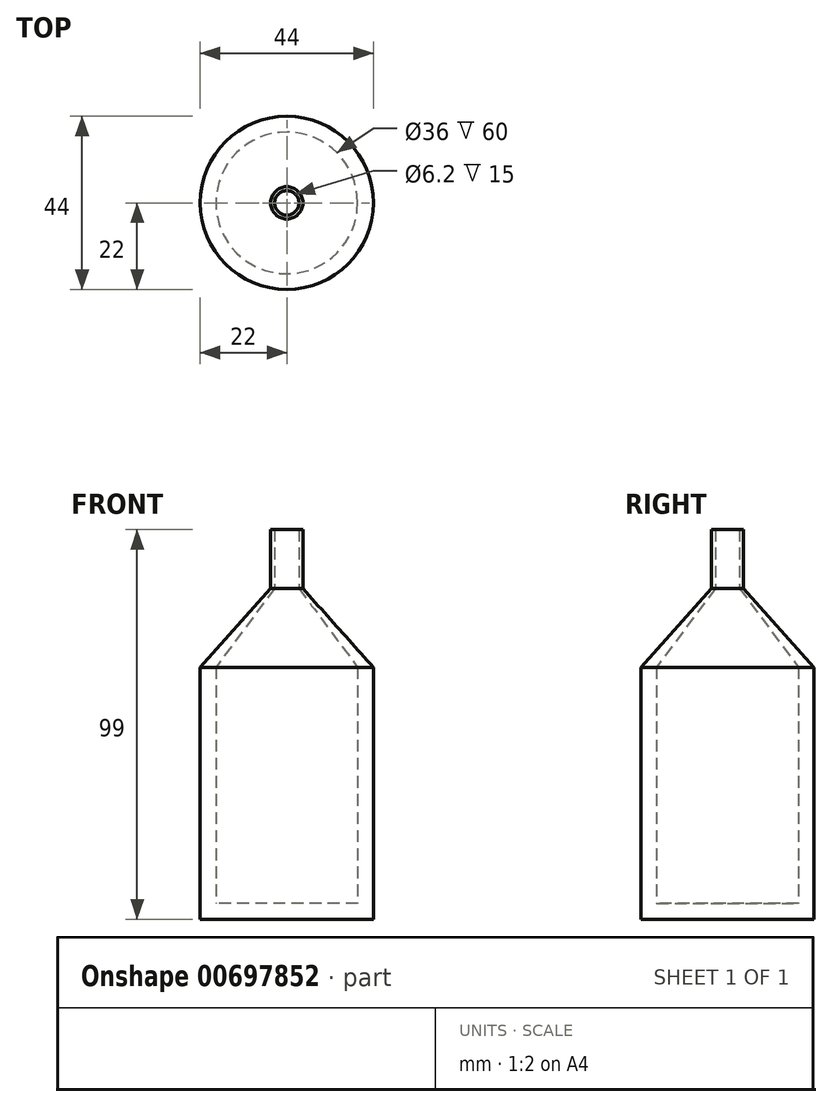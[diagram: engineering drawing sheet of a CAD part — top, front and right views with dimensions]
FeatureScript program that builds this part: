
annotation { "Feature Type Name" : "Feature", "Feature Type Description" : "" }
export const myFeature = defineFeature(function(context is Context, id is Id, definition is map)
    precondition{}
    {
        {
            assignVariable(context, id + "F0", {"name" : "W", "anyValue" : 2});
        }
        {
            var Q0;
            Q0=qCreatedBy(makeId("Top.planeOp"),FACE);
            var sketch = newSketch(context, id + "F1", { "sketchPlane" : qUnion([Q0])});
            skCircle(sketch, "E0", {"center": v(0, 0) * mm, "radius": 20 * mm, "construction": true});
            skArc(sketch, "E1.0", {"start": v(-11.23, -14.06) * mm, "mid": v(-6.89, -16.63) * mm, "end": v(-2, -17.89) * mm});
            skLineSegment(sketch, "E2", {"start": v(0, 0) * mm, "end": v(0, 18) * mm, "construction": true});
            skLineSegment(sketch, "E3", {"start": v(0, 0) * mm, "end": v(18, 0) * mm, "construction": true});
            skLineSegment(sketch, "E4", {"start": v(0, 0) * mm, "end": v(0, -18) * mm, "construction": true});
            skLineSegment(sketch, "E5", {"start": v(0, 0) * mm, "end": v(-18, 0) * mm, "construction": true});
            skLineSegment(sketch, "E6", {"start": v(0, 0) * mm, "end": v(-12.73, 12.73) * mm, "construction": true});
            skLineSegment(sketch, "E7", {"start": v(0, 0) * mm, "end": v(12.73, 12.73) * mm, "construction": true});
            skLineSegment(sketch, "E8", {"start": v(0, 0) * mm, "end": v(12.73, -12.73) * mm, "construction": true});
            skLineSegment(sketch, "E9", {"start": v(0, 0) * mm, "end": v(-12.73, -12.73) * mm, "construction": true});
            skCircle(sketch, "E10.0", {"center": v(0, 0) * mm, "radius": 22 * mm});
            skArc(sketch, "E11.0", {"start": v(-14.08, -16.9) * mm, "mid": v(-8.42, -20.33) * mm, "end": v(-2, -21.9) * mm});
            skCircle(sketch, "E12.0", {"center": v(0, 0) * mm, "radius": 18 * mm});
            skLineSegment(sketch, "E13.0", {"start": v(-17.89, 2) * mm, "end": v(-21.9, 2) * mm});
            skLineSegment(sketch, "E14.0", {"start": v(-17.89, -2) * mm, "end": v(-21.9, -2) * mm});
            skLineSegment(sketch, "E15.0", {"start": v(2, 17.89) * mm, "end": v(2, 21.9) * mm});
            skLineSegment(sketch, "E16.0", {"start": v(-2, 17.89) * mm, "end": v(-2, 21.9) * mm});
            skLineSegment(sketch, "E17.0", {"start": v(-11.23, 14.06) * mm, "end": v(-14.08, 16.9) * mm});
            skLineSegment(sketch, "E18.0", {"start": v(-14.06, 11.23) * mm, "end": v(-16.9, 14.08) * mm});
            skLineSegment(sketch, "E19.0", {"start": v(-14.06, -11.23) * mm, "end": v(-16.9, -14.08) * mm});
            skLineSegment(sketch, "E20.0", {"start": v(-11.23, -14.06) * mm, "end": v(-14.08, -16.9) * mm});
            skLineSegment(sketch, "E21.0", {"start": v(2, -17.89) * mm, "end": v(2, -21.9) * mm});
            skLineSegment(sketch, "E22.0", {"start": v(11.23, -14.06) * mm, "end": v(14.08, -16.9) * mm});
            skLineSegment(sketch, "E23.0", {"start": v(-2, -17.89) * mm, "end": v(-2, -21.9) * mm});
            skLineSegment(sketch, "E24.0", {"start": v(14.06, -11.23) * mm, "end": v(16.9, -14.08) * mm});
            skLineSegment(sketch, "E25.0", {"start": v(17.89, -2) * mm, "end": v(21.9, -2) * mm});
            skLineSegment(sketch, "E26.0", {"start": v(17.89, 2) * mm, "end": v(21.9, 2) * mm});
            skLineSegment(sketch, "E27.0", {"start": v(14.06, 11.23) * mm, "end": v(16.9, 14.08) * mm});
            skLineSegment(sketch, "E28.0", {"start": v(11.23, 14.06) * mm, "end": v(14.08, 16.9) * mm});
            skArc(sketch, "E29.trimOffspring", {"start": v(2, -17.89) * mm, "mid": v(6.89, -16.63) * mm, "end": v(11.23, -14.06) * mm});
            skArc(sketch, "E30.trimOffspring", {"start": v(2, -21.9) * mm, "mid": v(8.42, -20.33) * mm, "end": v(14.08, -16.9) * mm});
            skArc(sketch, "E31.trimOffspring", {"start": v(16.9, -14.08) * mm, "mid": v(20.33, -8.42) * mm, "end": v(21.9, -2) * mm});
            skArc(sketch, "E32.trimOffspring", {"start": v(14.06, -11.23) * mm, "mid": v(16.63, -6.89) * mm, "end": v(17.89, -2) * mm});
            skArc(sketch, "E33.trimOffspring", {"start": v(17.89, 2) * mm, "mid": v(16.63, 6.89) * mm, "end": v(14.06, 11.23) * mm});
            skArc(sketch, "E34.trimOffspring", {"start": v(21.9, 2) * mm, "mid": v(20.33, 8.42) * mm, "end": v(16.9, 14.08) * mm});
            skArc(sketch, "E35.trimOffspring", {"start": v(14.08, 16.9) * mm, "mid": v(8.42, 20.33) * mm, "end": v(2, 21.9) * mm});
            skArc(sketch, "E36.trimOffspring", {"start": v(11.23, 14.06) * mm, "mid": v(6.89, 16.63) * mm, "end": v(2, 17.89) * mm});
            skArc(sketch, "E37.trimOffspring", {"start": v(-2, 21.9) * mm, "mid": v(-8.42, 20.33) * mm, "end": v(-14.08, 16.9) * mm});
            skArc(sketch, "E38.trimOffspring", {"start": v(-2, 17.89) * mm, "mid": v(-6.89, 16.63) * mm, "end": v(-11.23, 14.06) * mm});
            skArc(sketch, "E39.trimOffspring", {"start": v(-14.06, 11.23) * mm, "mid": v(-16.63, 6.89) * mm, "end": v(-17.89, 2) * mm});
            skArc(sketch, "E40.trimOffspring", {"start": v(-16.9, 14.08) * mm, "mid": v(-20.33, 8.42) * mm, "end": v(-21.9, 2) * mm});
            skArc(sketch, "E41.trimOffspring", {"start": v(-17.89, -2) * mm, "mid": v(-16.63, -6.89) * mm, "end": v(-14.06, -11.23) * mm});
            skArc(sketch, "E42.trimOffspring", {"start": v(-21.9, -2) * mm, "mid": v(-20.33, -8.42) * mm, "end": v(-16.9, -14.08) * mm});
            skSolve(sketch);
        }
        {
            var Q0;
            Q0 = qSketchRegion(id + "F1", true);
            extrude(context, id + "F2", {"entities" : qUnion([Q0]), "depth" : (getVariable(context, 'W')) * mm, "offsetDistance" : 25 * mm});
        }
        {
            var Q0;
            Q0=qCreatedBy(makeId("Top.planeOp"),FACE);
            var sketch = newSketch(context, id + "F3", { "sketchPlane" : qUnion([Q0])});
            skCircle(sketch, "E43.0", {"center": v(0, 0) * mm, "radius": 22 * mm});
            skCircle(sketch, "E44.0", {"center": v(0, 0) * mm, "radius": 18 * mm});
            skSolve(sketch);
        }
        {
            var Q0;
            Q0 = qSketchRegion(id + "F3", true);
            extrude(context, id + "F4", {"entities" : qUnion([Q0]), "operationType" : NewBodyOperationType.ADD, "depth" : 60 * mm, "offsetDistance" : 25 * mm});
        }
        {
            var Q0;
            Q0=qCreatedBy(makeId("Top.planeOp"),FACE);
            var sketch = newSketch(context, id + "F5", { "sketchPlane" : qUnion([Q0])});
            skCircle(sketch, "E45.0", {"center": v(0, 0) * mm, "radius": 22 * mm});
            skSolve(sketch);
        }
        {
            var Q0;
            Q0 = qSketchRegion(id + "F5", true);
            extrude(context, id + "F6", {"entities" : qUnion([Q0]), "operationType" : NewBodyOperationType.ADD, "oppositeDirection" : true, "depth" : (getVariable(context, 'W') * 2) * mm, "offsetDistance" : 25 * mm});
        }
        {
            var Q0;
            Q0=makeQuery(id+"F4.opExtrude","CAP_FACE",FACE,{"disambiguationData":[OSD([sQuery(id+"F3.wireOp",EDGE,"E43.0"),sQuery(id+"F3.wireOp",EDGE,"E44.0")])],"isStart":false});
            cPlane(context, id + "F7", {"entities" : qUnion([Q0]), "cplaneType" : CPlaneType.OFFSET, "offset" : 20 * mm, "width" : 150 * mm, "height" : 150 * mm});
        }
        {
            var Q0;
            Q0=qCreatedBy(id+"F7.planeOp",FACE);
            var sketch = newSketch(context, id + "F8", { "sketchPlane" : qUnion([Q0])});
            skCircle(sketch, "E46", {"center": v(0, 0) * mm, "radius": 4.1 * mm});
            skSolve(sketch);
        }
        {
            var Q0;
            Q0=makeQuery(id+"F4.opExtrude","CAP_FACE",FACE,{"disambiguationData":[OSD([sQuery(id+"F3.wireOp",EDGE,"E43.0"),sQuery(id+"F3.wireOp",EDGE,"E44.0")])],"isStart":false});
            cPlane(context, id + "F9", {"entities" : qUnion([Q0]), "cplaneType" : CPlaneType.OFFSET, "offset" : 0 * mm, "width" : 150 * mm, "height" : 150 * mm});
        }
        {
            var Q0;
            Q0=qCreatedBy(id+"F9.planeOp",FACE);
            var sketch = newSketch(context, id + "F10", { "sketchPlane" : qUnion([Q0])});
            skCircle(sketch, "E47.0", {"center": v(0, 0) * mm, "radius": 22 * mm});
            skSolve(sketch);
        }
        {
            var Q1;
            Q1 = qSketchRegion(id + "F10", true);
            var Q2;
            Q2 = qSketchRegion(id + "F8", true);
            loft(context, id + "F11", {"operationType" : NewBodyOperationType.ADD, "sheetProfilesArray" : [{ "sheetProfileEntities" : qUnion([Q1]) }, { "sheetProfileEntities" : qUnion([Q2]) }]});
        }
        {
            var Q0;
            Q0=qCreatedBy(id+"F9.planeOp",FACE);
            var sketch = newSketch(context, id + "F12", { "sketchPlane" : qUnion([Q0])});
            skCircle(sketch, "E48.0", {"center": v(0, 0) * mm, "radius": 22 * mm, "construction": true});
            skCircle(sketch, "E49.0", {"center": v(0, 0) * mm, "radius": 18 * mm});
            skSolve(sketch);
        }
        {
            var Q0;
            Q0=qCreatedBy(id+"F7.planeOp",FACE);
            var sketch = newSketch(context, id + "F13", { "sketchPlane" : qUnion([Q0])});
            skCircle(sketch, "E50.0", {"center": v(0, 0) * mm, "radius": 4.1 * mm, "construction": true});
            skCircle(sketch, "E51.0", {"center": v(0, 0) * mm, "radius": 3.1 * mm});
            skSolve(sketch);
        }
        {
            var Q1;
            Q1 = qSketchRegion(id + "F12", true);
            var Q2;
            Q2 = qSketchRegion(id + "F13", true);
            loft(context, id + "F14", {"operationType" : NewBodyOperationType.REMOVE, "sheetProfilesArray" : [{ "sheetProfileEntities" : qUnion([Q1]) }, { "sheetProfileEntities" : qUnion([Q2]) }]});
        }
        {
            var Q0;
            Q0=makeQuery(id+"F11.opLoft","CAP_FACE",FACE,{"disambiguationData":[OSD([makeQuery(id+"F8.imprint","IMPRINT",FACE,{"disambiguationData":[TD([[makeQuery(id+"F8.imprint","IMPRINT",EDGE,{"derivedFrom":sQuery(id+"F8.wireOp",EDGE,"E46")}),1.0]])]})])],"isStart":true});
            extrude(context, id + "F15", {"entities" : qUnion([Q0]), "operationType" : NewBodyOperationType.ADD, "depth" : 15 * mm, "offsetDistance" : 25 * mm});
        }
    });
